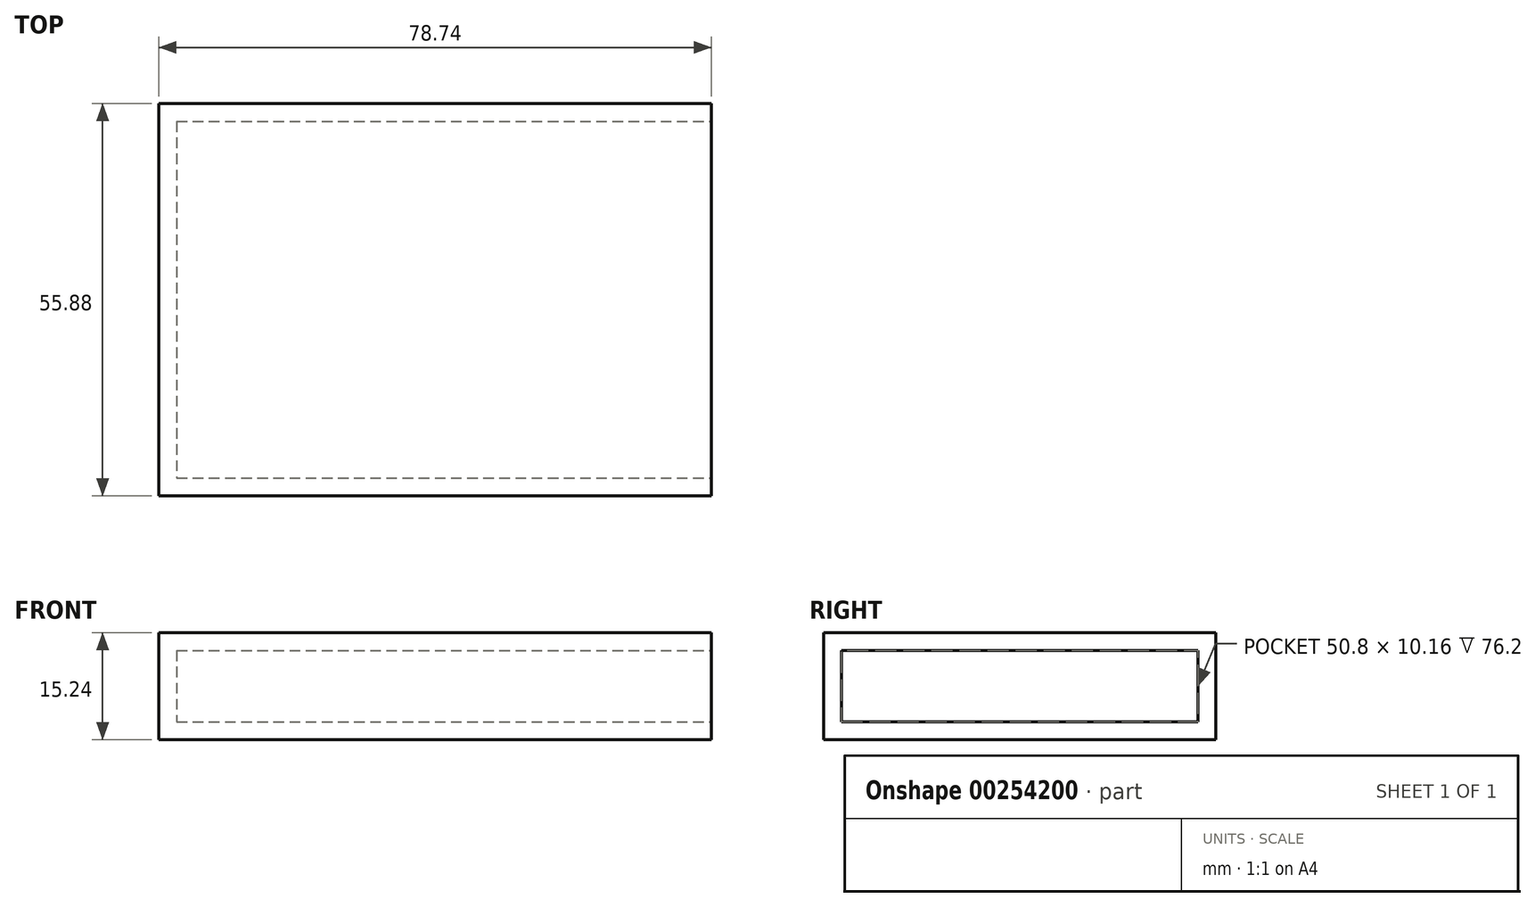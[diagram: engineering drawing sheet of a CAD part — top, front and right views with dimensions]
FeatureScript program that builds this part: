
annotation { "Feature Type Name" : "Feature", "Feature Type Description" : "" }
export const myFeature = defineFeature(function(context is Context, id is Id, definition is map)
    precondition{}
    {
        {
            var Q0;
            Q0=qCreatedBy(makeId("Top.planeOp"),FACE);
            var sketch = newSketch(context, id + "F0", { "sketchPlane" : qUnion([Q0])});
            skLineSegment(sketch, "E0.bottom", {"start": v(0, 55.88) * mm, "end": v(78.74, 55.88) * mm});
            skLineSegment(sketch, "E0.top", {"start": v(0, 0) * mm, "end": v(78.74, 0) * mm});
            skLineSegment(sketch, "E0.left", {"start": v(0, 55.88) * mm, "end": v(0, 0) * mm});
            skLineSegment(sketch, "E0.right", {"start": v(78.74, 55.88) * mm, "end": v(78.74, 0) * mm});
            skSolve(sketch);
        }
        {
            var Q0;
            Q0 = qSketchRegion(id + "F0", true);
            extrude(context, id + "F1", {"entities" : qUnion([Q0]), "depth" : 15.24 * mm});
        }
        {
            var Q0;
            Q0=makeQuery(id+"F1.opExtrude","SWEPT_FACE",FACE,{"disambiguationData":[OSD([sQuery(id+"F0.wireOp",EDGE,"E0.right")])]});
            shell(context, id + "F2", {"entities" : qUnion([Q0]), "thickness" : 2.54 * mm});
        }
    });
